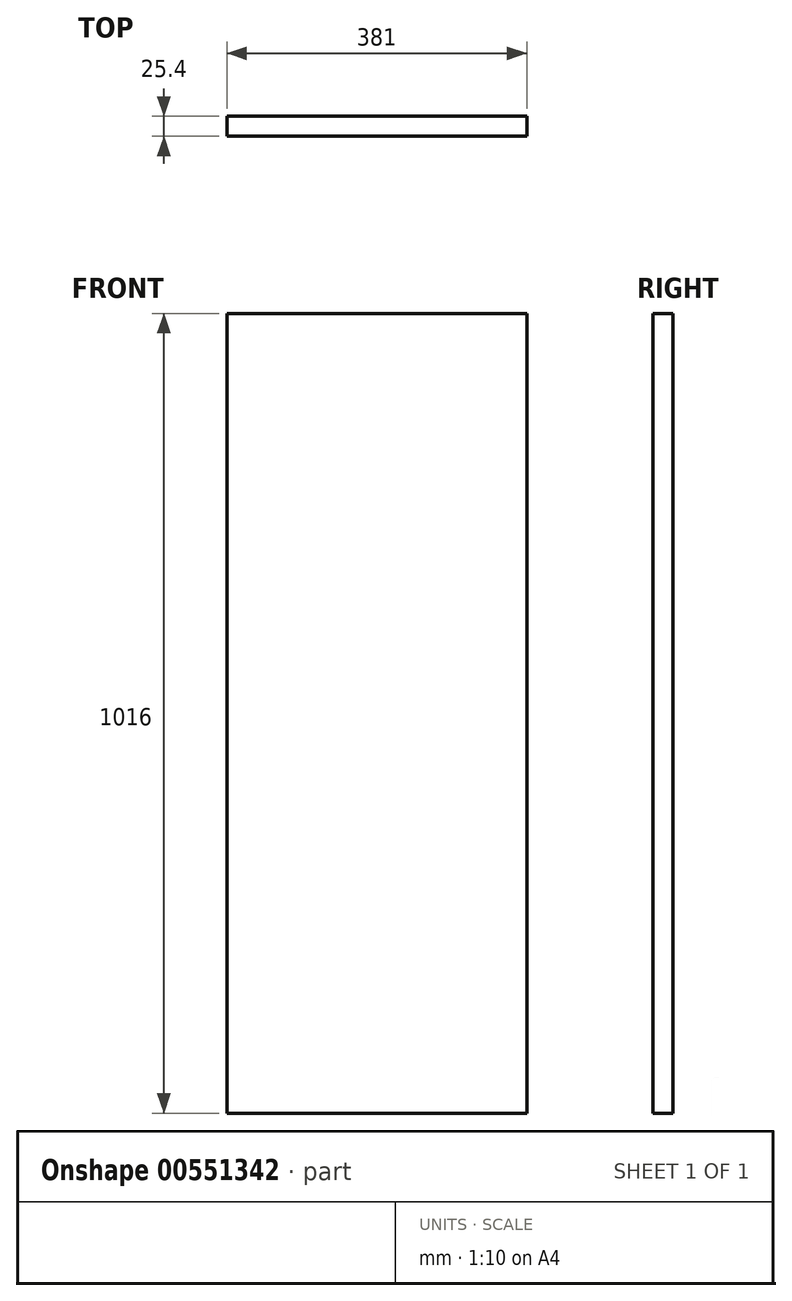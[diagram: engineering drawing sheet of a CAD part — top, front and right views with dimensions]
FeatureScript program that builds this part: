
annotation { "Feature Type Name" : "Feature", "Feature Type Description" : "" }
export const myFeature = defineFeature(function(context is Context, id is Id, definition is map)
    precondition{}
    {
        {
            var Q0;
            Q0=qCreatedBy(makeId("Front.planeOp"),FACE);
            var sketch = newSketch(context, id + "F0", { "sketchPlane" : qUnion([Q0])});
            skLineSegment(sketch, "E0.bottom", {"start": v(-195.4, 851.08) * mm, "end": v(185.6, 851.08) * mm});
            skLineSegment(sketch, "E0.top", {"start": v(-195.4, -164.92) * mm, "end": v(185.6, -164.92) * mm});
            skLineSegment(sketch, "E0.left", {"start": v(-195.4, 851.08) * mm, "end": v(-195.4, -164.92) * mm});
            skLineSegment(sketch, "E0.right", {"start": v(185.6, 851.08) * mm, "end": v(185.6, -164.92) * mm});
            skSolve(sketch);
        }
        {
            var Q0;
            Q0=makeQuery(id+"F0.imprint","IMPRINT",FACE,{"disambiguationData":[TD([[makeQuery(id+"F0.imprint","IMPRINT",EDGE,{"derivedFrom":sQuery(id+"F0.wireOp",EDGE,"E0.bottom")}),-1.0]])]});
            extrude(context, id + "F1", {"entities" : qUnion([Q0]), "depth" : 25.4 * mm, "offsetDistance" : 25.4 * mm});
        }
    });
